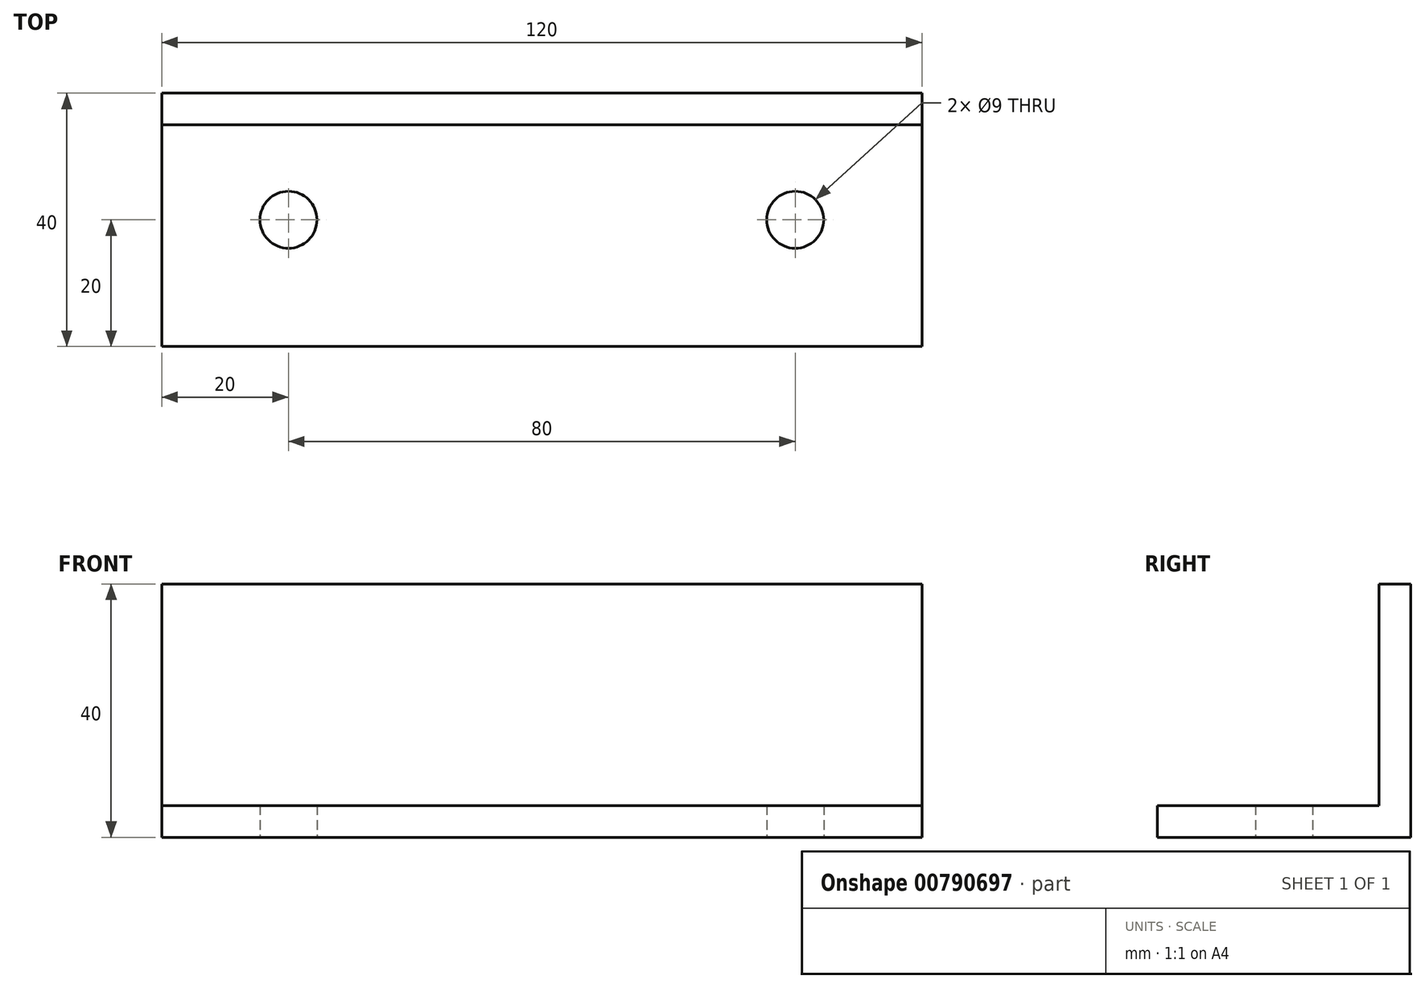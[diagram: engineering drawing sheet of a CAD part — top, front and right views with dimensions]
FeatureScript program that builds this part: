
annotation { "Feature Type Name" : "Feature", "Feature Type Description" : "" }
export const myFeature = defineFeature(function(context is Context, id is Id, definition is map)
    precondition{}
    {
        {
            var Q0;
            Q0=qCreatedBy(makeId("Right.planeOp"),FACE);
            var sketch = newSketch(context, id + "F0", { "sketchPlane" : qUnion([Q0])});
            skLineSegment(sketch, "E0", {"start": v(0, 0) * mm, "end": v(0, 40) * mm});
            skLineSegment(sketch, "E1", {"start": v(0, 0) * mm, "end": v(-40, 0) * mm});
            skLineSegment(sketch, "E2.0", {"start": v(-5, 5) * mm, "end": v(-40, 5) * mm});
            skLineSegment(sketch, "E2.1", {"start": v(-5, 5) * mm, "end": v(-5, 40) * mm});
            skLineSegment(sketch, "E3", {"start": v(-40, 0) * mm, "end": v(-40, 5) * mm});
            skLineSegment(sketch, "E4", {"start": v(-5, 40) * mm, "end": v(0, 40) * mm});
            skSolve(sketch);
        }
        {
            var Q0;
            Q0=makeQuery(id+"F0.imprint","IMPRINT",FACE,{"disambiguationData":[TD([[makeQuery(id+"F0.imprint","IMPRINT",EDGE,{"derivedFrom":sQuery(id+"F0.wireOp",EDGE,"E0")}),1.0]])]});
            extrude(context, id + "F1", {"entities" : qUnion([Q0]), "depth" : 120 * mm, "offsetDistance" : 25 * mm});
        }
        {
            var Q0;
            Q0=makeQuery(id+"F1.opExtrude","SWEPT_FACE",FACE,{"disambiguationData":[OSD([sQuery(id+"F0.wireOp",EDGE,"E1")])]});
            var sketch = newSketch(context, id + "F2", { "sketchPlane" : qUnion([Q0])});
            skCircle(sketch, "E5", {"center": v(100, 20) * mm, "radius": 4.5 * mm});
            skCircle(sketch, "E6", {"center": v(20, 20) * mm, "radius": 4.5 * mm});
            skSolve(sketch);
        }
        {
            var Q0;
            Q0=makeQuery(id+"F2.imprint","IMPRINT",FACE,{"disambiguationData":[TD([[makeQuery(id+"F2.imprint","IMPRINT",EDGE,{"derivedFrom":sQuery(id+"F2.wireOp",EDGE,"E6")}),1.0]])]});
            var Q1;
            Q1=makeQuery(id+"F2.imprint","IMPRINT",FACE,{"disambiguationData":[TD([[makeQuery(id+"F2.imprint","IMPRINT",EDGE,{"derivedFrom":sQuery(id+"F2.wireOp",EDGE,"E5")}),1.0]])]});
            extrude(context, id + "F3", {"entities" : qUnion([Q0, Q1]), "operationType" : NewBodyOperationType.REMOVE, "oppositeDirection" : true, "depth" : 25 * mm, "offsetDistance" : 25 * mm});
        }
    });
